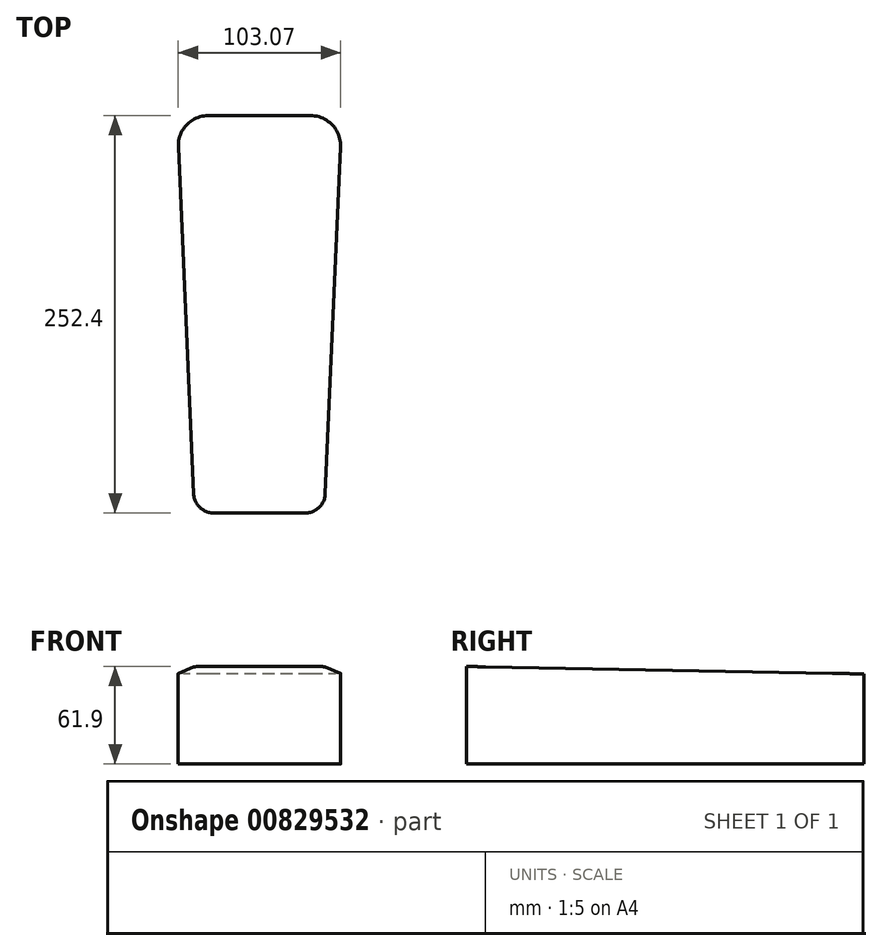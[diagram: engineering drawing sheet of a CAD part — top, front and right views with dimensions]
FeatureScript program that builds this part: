
annotation { "Feature Type Name" : "Feature", "Feature Type Description" : "" }
export const myFeature = defineFeature(function(context is Context, id is Id, definition is map)
    precondition{}
    {
        {
            var Q0;
            Q0=qCreatedBy(makeId("Top.planeOp"),FACE);
            var sketch = newSketch(context, id + "F0", { "sketchPlane" : qUnion([Q0])});
            skLineSegment(sketch, "E0", {"start": v(-0.53, 12.14) * mm, "end": v(-10.24, 232.51) * mm});
            skLineSegment(sketch, "E1", {"start": v(8.8, 252.4) * mm, "end": v(73.76, 252.4) * mm});
            skLineSegment(sketch, "E2", {"start": v(92.79, 232.51) * mm, "end": v(83.08, 12.14) * mm});
            skLineSegment(sketch, "E3", {"start": v(70.4, 0) * mm, "end": v(12.15, 0) * mm});
            skLineSegment(sketch, "E4", {"start": v(41.28, 0) * mm, "end": v(41.28, 200.86) * mm, "construction": true});
            skPoint(sketch, "E5.visualSharp", {"position": v(-11.11, 252.4) * mm});
            skArc(sketch, "E5.filletArc", {"start": v(8.8, 252.4) * mm, "mid": v(-4.97, 246.52) * mm, "end": v(-10.24, 232.51) * mm});
            skPoint(sketch, "E6.visualSharp", {"position": v(93.66, 252.4) * mm});
            skArc(sketch, "E6.filletArc", {"start": v(92.79, 232.51) * mm, "mid": v(87.52, 246.52) * mm, "end": v(73.76, 252.4) * mm});
            skPoint(sketch, "E7.visualSharp", {"position": v(82.55, 0) * mm});
            skArc(sketch, "E7.filletArc", {"start": v(70.4, 0) * mm, "mid": v(79.18, 3.52) * mm, "end": v(83.08, 12.14) * mm});
            skPoint(sketch, "E8.visualSharp", {"position": v(0, 0) * mm});
            skArc(sketch, "E8.filletArc", {"start": v(-0.53, 12.14) * mm, "mid": v(3.37, 3.52) * mm, "end": v(12.15, 0) * mm});
            skSolve(sketch);
        }
        {
            var Q0;
            Q0=makeQuery(id+"F0.imprint","IMPRINT",FACE,{"disambiguationData":[TD([[makeQuery(id+"F0.imprint","IMPRINT",EDGE,{"derivedFrom":sQuery(id+"F0.wireOp",EDGE,"E0")}),-1.0]])]});
            extrude(context, id + "F1", {"entities" : qUnion([Q0]), "depth" : 61.9 * mm, "offsetDistance" : 25.4 * mm});
        }
        {
            var Q0;
            Q0=qCreatedBy(makeId("Right.planeOp"),FACE);
            var sketch = newSketch(context, id + "F2", { "sketchPlane" : qUnion([Q0])});
            skLineSegment(sketch, "E9.bottom", {"start": v(0, 0) * mm, "end": v(252.4, 0) * mm, "construction": true});
            skLineSegment(sketch, "E9.top", {"start": v(0, 61.9) * mm, "end": v(252.4, 61.9) * mm, "construction": true});
            skLineSegment(sketch, "E9.left", {"start": v(0, 0) * mm, "end": v(0, 61.9) * mm, "construction": true});
            skLineSegment(sketch, "E9.right", {"start": v(252.4, 0) * mm, "end": v(252.4, 61.9) * mm, "construction": true});
            skPoint(sketch, "E10", {"position": v(252.4, 57.15) * mm});
            skLineSegment(sketch, "E11", {"start": v(252.4, 57.15) * mm, "end": v(252.4, 61.9) * mm});
            skLineSegment(sketch, "E12", {"start": v(0, 61.9) * mm, "end": v(252.4, 57.15) * mm});
            skLineSegment(sketch, "E13", {"start": v(252.4, 61.9) * mm, "end": v(0, 61.9) * mm});
            skSolve(sketch);
        }
        {
            var Q0;
            Q0=makeQuery(id+"F2.imprint","IMPRINT",FACE,{"disambiguationData":[TD([[makeQuery(id+"F2.imprint","IMPRINT",EDGE,{"derivedFrom":sQuery(id+"F2.wireOp",EDGE,"E11")}),1.0]])]});
            extrude(context, id + "F3", {"entities" : qUnion([Q0]), "operationType" : NewBodyOperationType.REMOVE, "endBound" : BoundingType.THROUGH_ALL, "depth" : 25.4 * mm, "offsetDistance" : 25.4 * mm});
        }
        {
            var Q0;
            Q0 = qSketchRegion(id + "F2", true);
            extrude(context, id + "F4", {"entities" : qUnion([Q0]), "operationType" : NewBodyOperationType.REMOVE, "oppositeDirection" : true, "depth" : 25.4 * mm, "offsetDistance" : 25.4 * mm});
        }
    });
